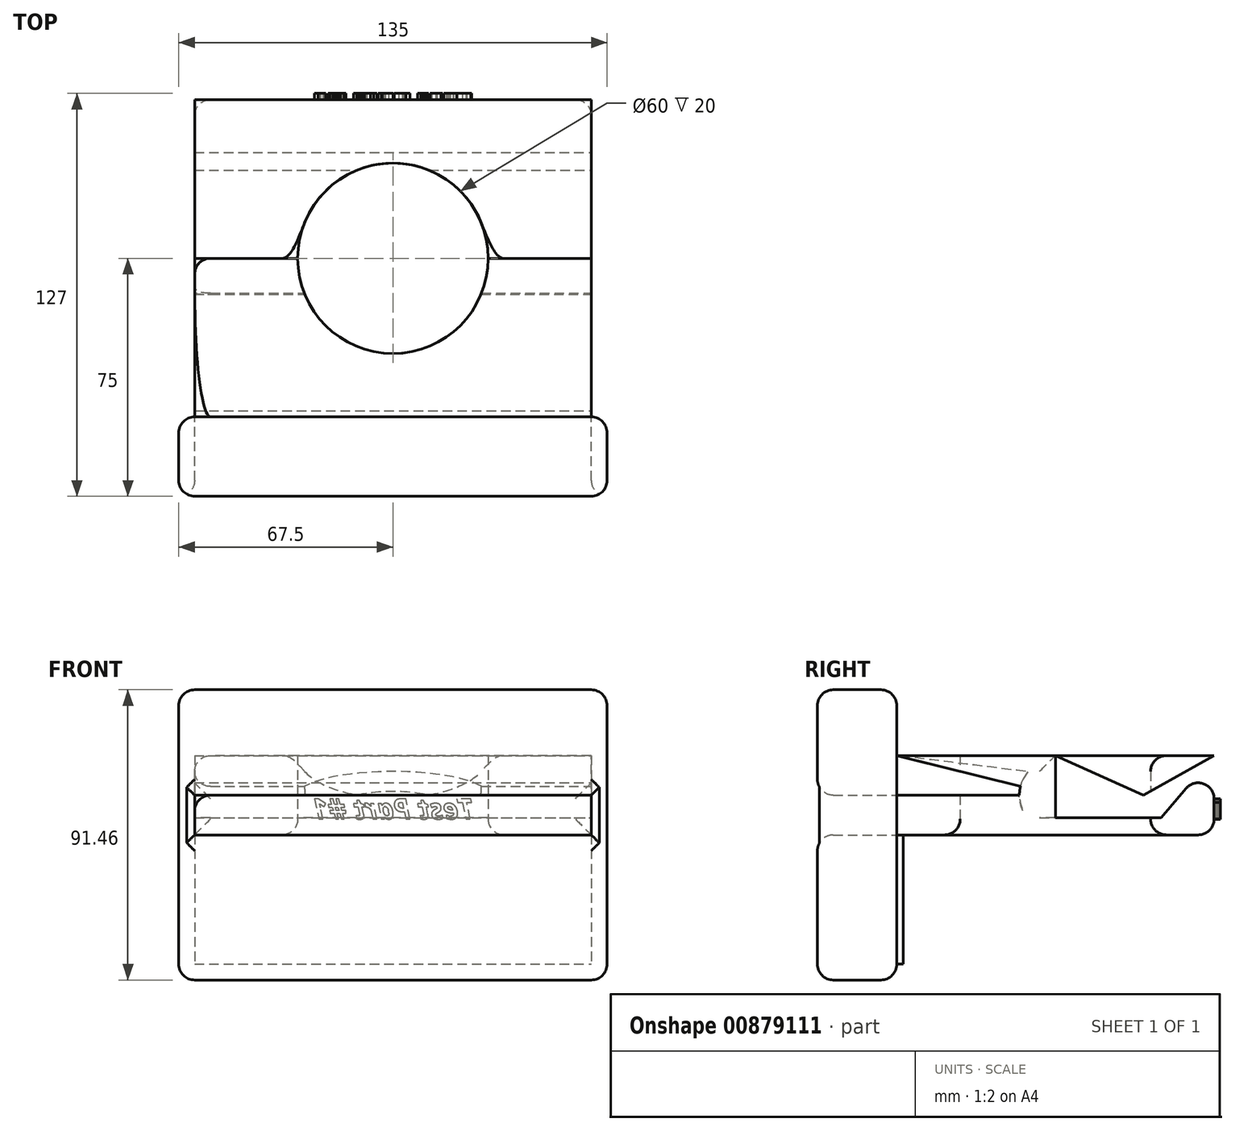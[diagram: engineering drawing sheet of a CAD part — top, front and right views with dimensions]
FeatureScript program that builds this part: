
annotation { "Feature Type Name" : "Feature", "Feature Type Description" : "" }
export const myFeature = defineFeature(function(context is Context, id is Id, definition is map)
    precondition{}
    {
        {
            var Q0;
            Q0=qCreatedBy(makeId("Top.planeOp"),FACE);
            var sketch = newSketch(context, id + "F0", { "sketchPlane" : qUnion([Q0])});
            skLineSegment(sketch, "E0.bottom", {"start": v(-62.5, -50) * mm, "end": v(62.5, -50) * mm});
            skLineSegment(sketch, "E0.top", {"start": v(-62.5, 50) * mm, "end": v(62.5, 50) * mm});
            skLineSegment(sketch, "E0.left", {"start": v(-62.5, -50) * mm, "end": v(-62.5, 50) * mm});
            skLineSegment(sketch, "E0.right", {"start": v(62.5, -50) * mm, "end": v(62.5, 50) * mm});
            skPoint(sketch, "E0.middle", {"position": v(0, 0) * mm});
            skCircle(sketch, "E1", {"center": v(0, 0) * mm, "radius": 30 * mm});
            skSolve(sketch);
        }
        {
            var Q0;
            Q0 = qSketchRegion(id + "F0", true);
            extrude(context, id + "F1", {"entities" : qUnion([Q0]), "depth" : 25 * mm, "offsetDistance" : 25 * mm});
        }
        {
            var Q0;
            Q0=makeQuery(id+"F1.opExtrude","SWEPT_FACE",FACE,{"disambiguationData":[OSD([sQuery(id+"F0.wireOp",EDGE,"E0.right")])]});
            var sketch = newSketch(context, id + "F2", { "sketchPlane" : qUnion([Q0])});
            skCircle(sketch, "E2", {"center": v(0, 12.5) * mm, "radius": 11.35 * mm});
            skPoint(sketch, "E2.centerSnap0", {"position": v(-50, 12.5) * mm});
            skLineSegment(sketch, "E3", {"start": v(-50, 25) * mm, "end": v(0, 12.5) * mm});
            skLineSegment(sketch, "E4", {"start": v(-50, 12.5) * mm, "end": v(0, 12.5) * mm});
            skLineSegment(sketch, "E5", {"start": v(50, 0) * mm, "end": v(0, 12.5) * mm});
            skLineSegment(sketch, "E6", {"start": v(50, 12.5) * mm, "end": v(36.91, 3.27) * mm});
            skSolve(sketch);
        }
        {
            var Q0;
            {var subQ0=sQuery(id+"F2.wireOp",EDGE,"E4");var subQ1=sQuery(id+"F2.wireOp",EDGE,"E2");var subQ2=makeQuery(id+"F2.imprint","INTERSECT",VERTEX,{"derivedFrom":[subQ1,subQ0]});Q0=makeQuery(id+"F2.imprint","IMPRINT",FACE,{"disambiguationData":[TD([[makeQuery(id+"F2.imprint","IMPRINT",EDGE,{"disambiguationData":[TD([[subQ2,1.0]])],"derivedFrom":subQ1}),-1.0]])]});}
            extrude(context, id + "F3", {"entities" : qUnion([Q0]), "operationType" : NewBodyOperationType.REMOVE, "oppositeDirection" : true, "depth" : 130.6 * mm, "offsetDistance" : 25 * mm});
        }
        {
            var Q0;
            Q0=makeQuery(id+"F1.opExtrude","SWEPT_FACE",FACE,{"disambiguationData":[OSD([sQuery(id+"F0.wireOp",EDGE,"E0.right")])]});
            var sketch = newSketch(context, id + "F4", { "sketchPlane" : qUnion([Q0])});
            skLineSegment(sketch, "E7", {"start": v(0, 25) * mm, "end": v(27.77, 12.57) * mm});
            skLineSegment(sketch, "E8", {"start": v(27.77, 12.57) * mm, "end": v(50, 25) * mm});
            skLineSegment(sketch, "E9", {"start": v(50, 25) * mm, "end": v(33.3, 5.39) * mm});
            skLineSegment(sketch, "E10", {"start": v(33.3, 5.39) * mm, "end": v(0, 5.39) * mm});
            skLineSegment(sketch, "E11", {"start": v(0, 5.39) * mm, "end": v(0, 25) * mm});
            skSolve(sketch);
        }
        {
            var Q0;
            Q0=makeQuery(id+"F4.imprint","IMPRINT",FACE,{"disambiguationData":[TD([[makeQuery(id+"F4.imprint","IMPRINT",EDGE,{"derivedFrom":sQuery(id+"F4.wireOp",EDGE,"E7")}),-1.0]])]});
            extrude(context, id + "F5", {"entities" : qUnion([Q0]), "operationType" : NewBodyOperationType.REMOVE, "oppositeDirection" : true, "depth" : 133.6 * mm, "offsetDistance" : 25 * mm});
        }
        {
            var Q0;
            Q0=makeQuery(id+"F1.opExtrude","SWEPT_FACE",FACE,{"disambiguationData":[OSD([sQuery(id+"F0.wireOp",EDGE,"E0.bottom")])]});
            var sketch = newSketch(context, id + "F6", { "sketchPlane" : qUnion([Q0])});
            skLineSegment(sketch, "E12.bottom", {"start": v(-67.5, 45.73) * mm, "end": v(67.5, 45.73) * mm});
            skLineSegment(sketch, "E12.top", {"start": v(-67.5, -45.73) * mm, "end": v(67.5, -45.73) * mm});
            skLineSegment(sketch, "E12.left", {"start": v(-67.5, 45.73) * mm, "end": v(-67.5, -45.73) * mm});
            skLineSegment(sketch, "E12.right", {"start": v(67.5, 45.73) * mm, "end": v(67.5, -45.73) * mm});
            skPoint(sketch, "E12.middle", {"position": v(0, 0) * mm});
            skSolve(sketch);
        }
        {
            var Q0;
            Q0=makeQuery(id+"F6.imprint","IMPRINT",FACE,{"disambiguationData":[TD([[makeQuery(id+"F6.imprint","IMPRINT",EDGE,{"derivedFrom":sQuery(id+"F6.wireOp",EDGE,"E12.bottom")}),-1.0]])]});
            extrude(context, id + "F7", {"entities" : qUnion([Q0]), "depth" : 25 * mm, "offsetDistance" : 25 * mm});
        }
        {
            var Q0;
            Q0=makeQuery(id+"F7.opExtrude","CAP_EDGE",EDGE,{"disambiguationData":[OSD([sQuery(id+"F6.wireOp",EDGE,"E12.left")])],"isStart":true});
            var Q1;
            Q1=makeQuery(id+"F7.opExtrude","CAP_EDGE",EDGE,{"disambiguationData":[OSD([sQuery(id+"F6.wireOp",EDGE,"E12.top")])],"isStart":true});
            var Q2;
            Q2=makeQuery(id+"F7.opExtrude","CAP_EDGE",EDGE,{"disambiguationData":[OSD([sQuery(id+"F6.wireOp",EDGE,"E12.left")])],"isStart":false});
            var Q3;
            Q3=makeQuery(id+"F7.opExtrude","SWEPT_EDGE",EDGE,{"disambiguationData":[OSD([sQuery(id+"F6.wireOp",EDGE,"E12.bottom"),sQuery(id+"F6.wireOp",EDGE,"E12.left")])]});
            var Q4;
            Q4=makeQuery(id+"F7.opExtrude","SWEPT_EDGE",EDGE,{"disambiguationData":[OSD([sQuery(id+"F6.wireOp",EDGE,"E12.top"),sQuery(id+"F6.wireOp",EDGE,"E12.left")])]});
            var Q5;
            Q5=makeQuery(id+"F7.opExtrude","SWEPT_EDGE",EDGE,{"disambiguationData":[OSD([sQuery(id+"F6.wireOp",EDGE,"E12.bottom"),sQuery(id+"F6.wireOp",EDGE,"E12.right")])]});
            var Q6;
            Q6=makeQuery(id+"F7.opExtrude","CAP_EDGE",EDGE,{"disambiguationData":[OSD([sQuery(id+"F6.wireOp",EDGE,"E12.right")])],"isStart":false});
            var Q7;
            Q7=makeQuery(id+"F7.opExtrude","CAP_EDGE",EDGE,{"disambiguationData":[OSD([sQuery(id+"F6.wireOp",EDGE,"E12.right")])],"isStart":true});
            var Q8;
            Q8=makeQuery(id+"F7.opExtrude","SWEPT_EDGE",EDGE,{"disambiguationData":[OSD([sQuery(id+"F6.wireOp",EDGE,"E12.top"),sQuery(id+"F6.wireOp",EDGE,"E12.right")])]});
            var Q9;
            Q9=makeQuery(id+"F7.opExtrude","CAP_EDGE",EDGE,{"disambiguationData":[OSD([sQuery(id+"F6.wireOp",EDGE,"E12.bottom")])],"isStart":true});
            var Q10;
            Q10=makeQuery(id+"F7.opExtrude","CAP_EDGE",EDGE,{"disambiguationData":[OSD([sQuery(id+"F6.wireOp",EDGE,"E12.bottom")])],"isStart":false});
            var Q11;
            Q11=makeQuery(id+"F1.opExtrude","CAP_EDGE",EDGE,{"disambiguationData":[OSD([sQuery(id+"F0.wireOp",EDGE,"E1")])],"isStart":true});
            var Q12;
            {var subQ0=sQuery(id+"F0.wireOp",EDGE,"E1");Q12=makeQuery(id+"F5.boolean.opBoolean","SPLIT",EDGE,{"disambiguationData":[TD([makeQuery(id+"F5.opExtrude","SWEPT_FACE",FACE,{"disambiguationData":[OSD([sQuery(id+"F4.wireOp",EDGE,"E7")])]})])],"derivedFrom":makeQuery(id+"F1.opExtrude","CAP_EDGE",EDGE,{"disambiguationData":[OSD([subQ0])],"isStart":false})});}
            var Q13;
            Q13=makeQuery(id+"F7.opExtrude","CAP_EDGE",EDGE,{"disambiguationData":[OSD([sQuery(id+"F6.wireOp",EDGE,"E12.top")])],"isStart":false});
            var Q14;
            {var subQ0=sQuery(id+"F0.wireOp",EDGE,"E0.top");var subQ1=sQuery(id+"F4.wireOp",EDGE,"E9");Q14=makeQuery(id+"F5.boolean.opBoolean","MERGE",EDGE,{"disambiguationData":[topologyDisambiguationEdgeConnected([makeQuery(id+"F1.opExtrude","SWEPT_FACE",FACE,{"disambiguationData":[OSD([subQ0])]})])],"derivedFrom":[makeQuery(id+"F1.opExtrude","CAP_EDGE",EDGE,{"disambiguationData":[OSD([subQ0])],"isStart":false})],"fromTools":[makeQuery(id+"F5.opExtrude","SWEPT_EDGE",EDGE,{"disambiguationData":[OSD([subQ0,sQuery(id+"F0.wireOp",EDGE,"E0.right"),sQuery(id+"F4.wireOp",EDGE,"E8"),subQ1])]})]});}
            var Q15;
            Q15=makeQuery(id+"F1.opExtrude","SWEPT_EDGE",EDGE,{"disambiguationData":[OSD([sQuery(id+"F0.wireOp",EDGE,"E0.top"),sQuery(id+"F0.wireOp",EDGE,"E0.left")])]});
            var Q16;
            Q16=makeQuery(id+"F1.opExtrude","CAP_EDGE",EDGE,{"disambiguationData":[OSD([sQuery(id+"F0.wireOp",EDGE,"E0.top")])],"isStart":true});
            var Q17;
            Q17=makeQuery(id+"F1.opExtrude","SWEPT_EDGE",EDGE,{"disambiguationData":[OSD([sQuery(id+"F0.wireOp",EDGE,"E0.top"),sQuery(id+"F0.wireOp",EDGE,"E0.right")])]});
            var Q18;
            Q18=makeQuery(id+"F5.boolean.opBoolean","INTERSECT",EDGE,{"derivedFrom":[makeQuery(id+"F1.opExtrude","SWEPT_FACE",FACE,{"disambiguationData":[OSD([sQuery(id+"F0.wireOp",EDGE,"E0.left")])]}),makeQuery(id+"F5.opExtrude","SWEPT_FACE",FACE,{"disambiguationData":[OSD([sQuery(id+"F4.wireOp",EDGE,"E11")])]})]});
            var Q19;
            Q19=makeQuery(id+"F3.boolean.opBoolean","INTERSECT",EDGE,{"derivedFrom":[makeQuery(id+"F1.opExtrude","SWEPT_FACE",FACE,{"disambiguationData":[OSD([sQuery(id+"F0.wireOp",EDGE,"E0.left")])]}),makeQuery(id+"F3.opExtrude","SWEPT_FACE",FACE,{"disambiguationData":[OSD([sQuery(id+"F2.wireOp",EDGE,"E3")])]})]});
            var Q20;
            {var subQ0=sQuery(id+"F0.wireOp",EDGE,"E0.left");Q20=makeQuery(id+"F5.boolean.opBoolean","SPLIT",EDGE,{"disambiguationData":[TD([makeQuery(id+"F3.boolean.opBoolean","COPY",FACE,{"derivedFrom":makeQuery(id+"F3.opExtrude","SWEPT_FACE",FACE,{"disambiguationData":[OSD([sQuery(id+"F2.wireOp",EDGE,"E3")])]})})])],"derivedFrom":makeQuery(id+"F1.opExtrude","CAP_EDGE",EDGE,{"disambiguationData":[OSD([subQ0])],"isStart":false})});}
            var Q21;
            Q21=makeQuery(id+"F3.boolean.opBoolean","INTERSECT",EDGE,{"derivedFrom":[makeQuery(id+"F1.opExtrude","SWEPT_FACE",FACE,{"disambiguationData":[OSD([sQuery(id+"F0.wireOp",EDGE,"E0.left")])]}),makeQuery(id+"F3.opExtrude","SWEPT_FACE",FACE,{"disambiguationData":[OSD([sQuery(id+"F2.wireOp",EDGE,"E4")])]})]});
            var Q22;
            Q22=makeQuery(id+"F7.opExtrude","CAP_EDGE",EDGE,{"disambiguationData":[OSD([sQuery(id+"F0.wireOp",EDGE,"E0.bottom")])],"isStart":false});
            var Q23;
            Q23=makeQuery(id+"F7.opExtrude","CAP_EDGE",EDGE,{"disambiguationData":[OSD([sQuery(id+"F0.wireOp",EDGE,"E0.bottom"),sQuery(id+"F0.wireOp",EDGE,"E0.right"),sQuery(id+"F2.wireOp",EDGE,"E4")])],"isStart":false});
            var Q24;
            Q24=makeQuery(id+"F7.opExtrude","CAP_EDGE",EDGE,{"disambiguationData":[OSD([sQuery(id+"F0.wireOp",EDGE,"E0.bottom"),sQuery(id+"F0.wireOp",EDGE,"E0.left")])],"isStart":false});
            var Q25;
            Q25=makeQuery(id+"F7.opExtrude","CAP_EDGE",EDGE,{"disambiguationData":[OSD([sQuery(id+"F0.wireOp",EDGE,"E0.bottom"),sQuery(id+"F0.wireOp",EDGE,"E0.right")])],"isStart":false});
            fillet(context, id + "F8", {"entities" : qUnion([Q0, Q1, Q2, Q3, Q4, Q5, Q6, Q7, Q8, Q9, Q10, Q11, Q12, Q13, Q14, Q15, Q16, Q17, Q18, Q19, Q20, Q21, Q22, Q23, Q24, Q25]), "radius" : 5 * mm, "tangentPropagation" : true, "allowEdgeOverflow" : false});
        }
        {
            var Q0;
            Q0=makeQuery(id+"F1.opExtrude","SWEPT_FACE",FACE,{"disambiguationData":[OSD([sQuery(id+"F0.wireOp",EDGE,"E0.top")])]});
            var sketch = newSketch(context, id + "F9", { "sketchPlane" : qUnion([Q0])});
            skText(sketch, "E13", { "text": "Test Part #1", "fontName": "OpenSans-BoldItalic.ttf"});
            const initialGuessF9  = {"E13": [-0.0255, 0.005, 1, 0, 0.00642]};
            skSetInitialGuess(sketch, initialGuessF9);
            skSolve(sketch);
        }
        {
            var Q0;
            Q0=makeQuery(id+"F8.opFillet","SPLIT",FACE,{"disambiguationData":[OD(0.0)],"derivedFrom":makeQuery(id+"F7.opExtrude","CAP_FACE",FACE,{"disambiguationData":[OSD([sQuery(id+"F0.wireOp",EDGE,"E0.bottom"),sQuery(id+"F0.wireOp",EDGE,"E0.left"),sQuery(id+"F0.wireOp",EDGE,"E0.right"),sQuery(id+"F2.wireOp",EDGE,"E4"),sQuery(id+"F6.wireOp",EDGE,"E12.bottom"),sQuery(id+"F6.wireOp",EDGE,"E12.top"),sQuery(id+"F6.wireOp",EDGE,"E12.left"),sQuery(id+"F6.wireOp",EDGE,"E12.right")])],"isStart":true})});
            var Q1;
            Q1 = qSketchRegion(id + "F9", true);
            extrude(context, id + "F10", {"entities" : qUnion([Q0, Q1]), "depth" : 2 * mm, "offsetDistance" : 25 * mm});
        }
    });
